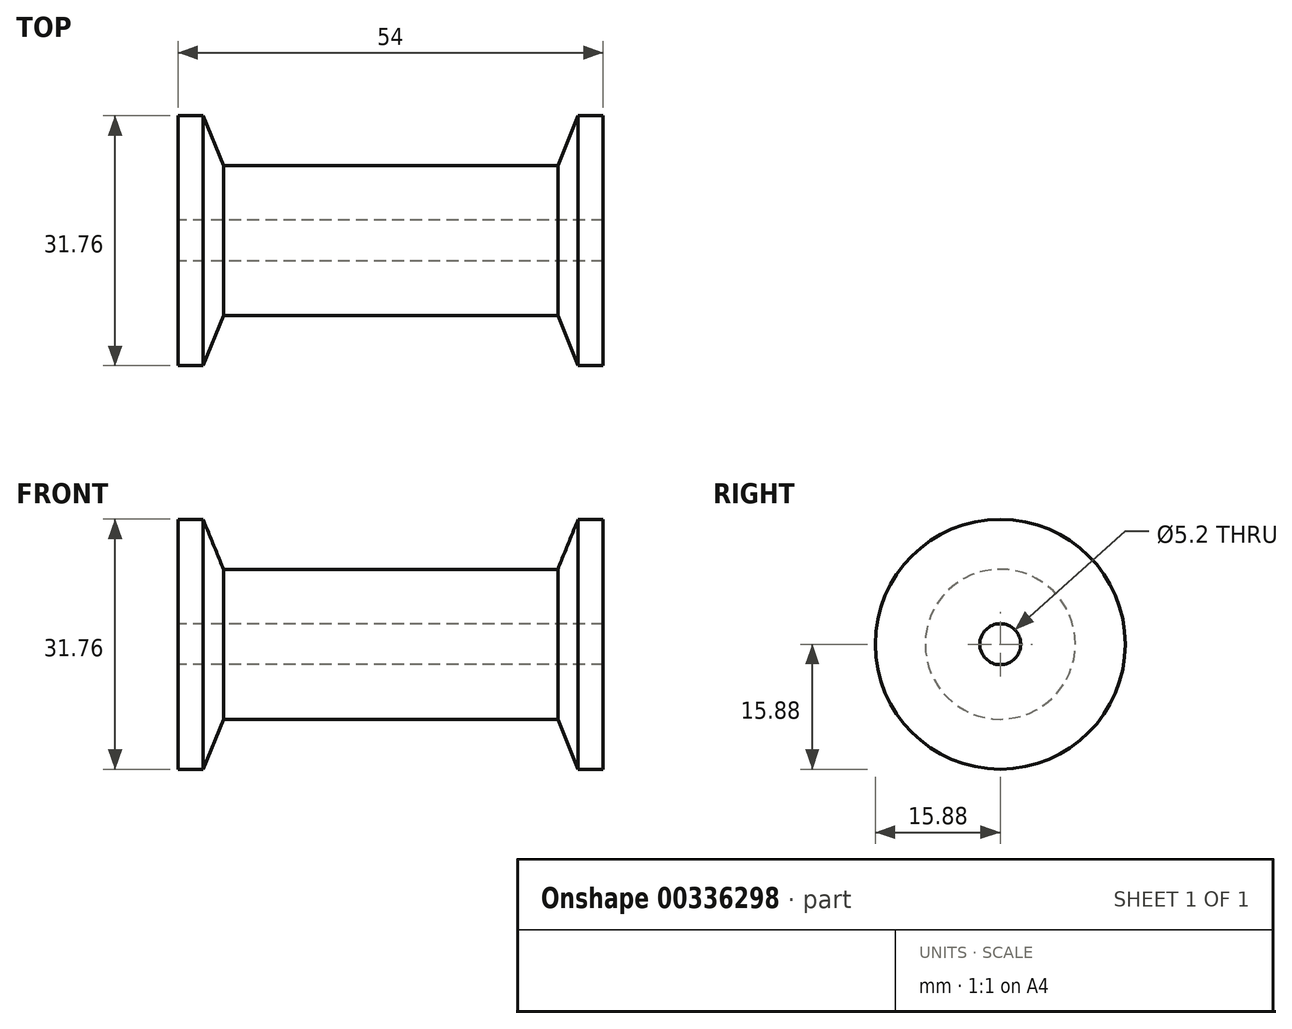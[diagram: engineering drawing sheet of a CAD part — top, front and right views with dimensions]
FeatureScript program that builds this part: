
annotation { "Feature Type Name" : "Feature", "Feature Type Description" : "" }
export const myFeature = defineFeature(function(context is Context, id is Id, definition is map)
    precondition{}
    {
        {
            var Q0;
            Q0=qCreatedBy(makeId("Front.planeOp"),FACE);
            var sketch = newSketch(context, id + "F0", { "sketchPlane" : qUnion([Q0])});
            skLineSegment(sketch, "E0", {"start": v(0, 0) * mm, "end": v(54, 0) * mm});
            skLineSegment(sketch, "E1", {"start": v(54, 0) * mm, "end": v(54, 2.6) * mm});
            skLineSegment(sketch, "E2", {"start": v(54, 2.6) * mm, "end": v(0, 2.6) * mm});
            skLineSegment(sketch, "E3", {"start": v(0, 2.6) * mm, "end": v(0, 0) * mm});
            skLineSegment(sketch, "E4", {"start": v(0, 0) * mm, "end": v(0, 15.88) * mm});
            skLineSegment(sketch, "E5", {"start": v(54, 0) * mm, "end": v(54, 15.87) * mm});
            skLineSegment(sketch, "E6", {"start": v(54, 15.87) * mm, "end": v(50.83, 15.87) * mm});
            skLineSegment(sketch, "E7", {"start": v(54, 0) * mm, "end": v(54, 9.53) * mm});
            skLineSegment(sketch, "E8", {"start": v(54, 9.53) * mm, "end": v(0, 9.52) * mm});
            skLineSegment(sketch, "E9", {"start": v(0, 9.52) * mm, "end": v(0, 0) * mm});
            skLineSegment(sketch, "E10", {"start": v(0, 15.88) * mm, "end": v(3.18, 15.88) * mm});
            skLineSegment(sketch, "E11", {"start": v(3.18, 15.88) * mm, "end": v(5.77, 9.52) * mm});
            skLineSegment(sketch, "E12", {"start": v(50.82, 15.88) * mm, "end": v(48.23, 9.53) * mm});
            skSolve(sketch);
        }
        {
            var Q0;
            {var subQ0=sQuery(id+"F0.wireOp",EDGE,"E4");Q0=makeQuery(id+"F0.imprint","IMPRINT",FACE,{"disambiguationData":[TD([[makeQuery(id+"F0.imprint","IMPRINT",EDGE,{"derivedFrom":subQ0}),-1.0]])]});}
            var Q1;
            {var subQ5=sQuery(id+"F0.wireOp",EDGE,"E2");Q1=makeQuery(id+"F0.imprint","IMPRINT",FACE,{"disambiguationData":[TD([[makeQuery(id+"F0.imprint","IMPRINT",EDGE,{"derivedFrom":subQ5}),-1.0]])]});}
            var Q2;
            {var subQ0=sQuery(id+"F0.wireOp",EDGE,"E5");Q2=makeQuery(id+"F0.imprint","IMPRINT",FACE,{"disambiguationData":[TD([[makeQuery(id+"F0.imprint","IMPRINT",EDGE,{"derivedFrom":subQ0}),1.0]])]});}
            var Q3;
            Q3=sQuery(id+"F0.wireOp",EDGE,"E0");
            revolve(context, id + "F1", {"entities" : qUnion([Q0, Q1, Q2]), "axis" : qUnion([Q3]), "revolveType" : RevolveType.FULL});
        }
    });
